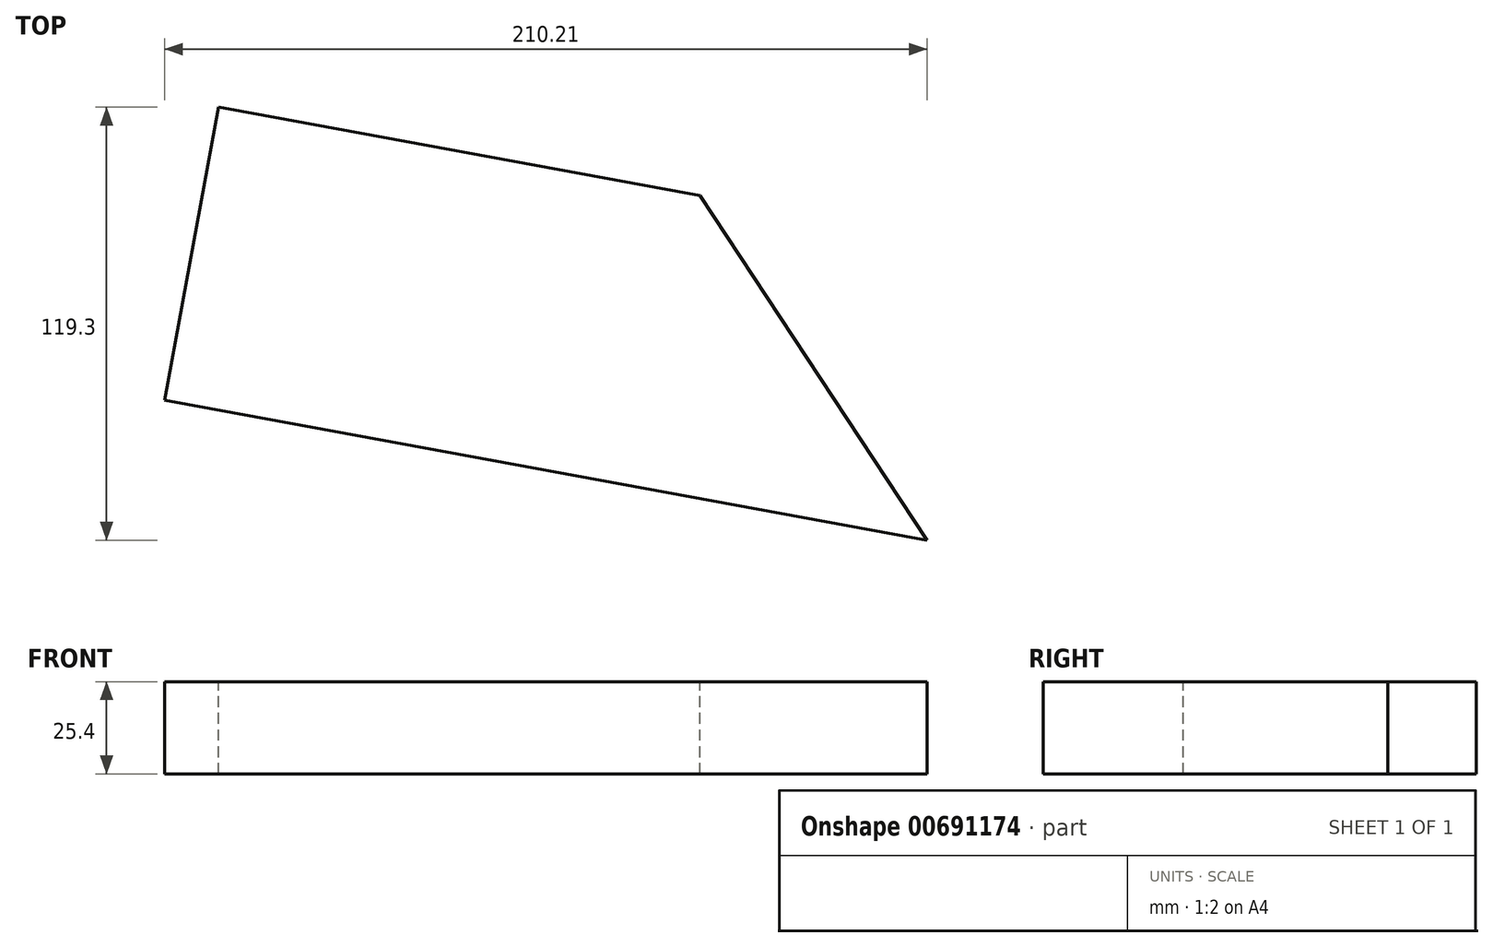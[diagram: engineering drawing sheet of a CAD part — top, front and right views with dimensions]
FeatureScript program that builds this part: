
annotation { "Feature Type Name" : "Feature", "Feature Type Description" : "" }
export const myFeature = defineFeature(function(context is Context, id is Id, definition is map)
    precondition{}
    {
        {
            var Q0;
            Q0=qCreatedBy(makeId("Top.planeOp"),FACE);
            var sketch = newSketch(context, id + "F0", { "sketchPlane" : qUnion([Q0])});
            skLineSegment(sketch, "E0", {"start": v(129, -71.87) * mm, "end": v(-81.2, -33.3) * mm});
            skLineSegment(sketch, "E1", {"start": v(-81.2, -33.3) * mm, "end": v(-66.4, 47.43) * mm});
            skLineSegment(sketch, "E2", {"start": v(-66.4, 47.43) * mm, "end": v(66.37, 23.08) * mm});
            skLineSegment(sketch, "E3", {"start": v(66.37, 23.08) * mm, "end": v(129, -71.87) * mm});
            skSolve(sketch);
        }
        {
            var Q0;
            Q0=makeQuery(id+"F0.imprint","IMPRINT",FACE,{"disambiguationData":[TD([[makeQuery(id+"F0.imprint","IMPRINT",EDGE,{"derivedFrom":sQuery(id+"F0.wireOp",EDGE,"E0")}),-1.0]])]});
            extrude(context, id + "F1", {"entities" : qUnion([Q0]), "oppositeDirection" : true, "depth" : 25.4 * mm, "offsetDistance" : 25.4 * mm});
        }
    });
